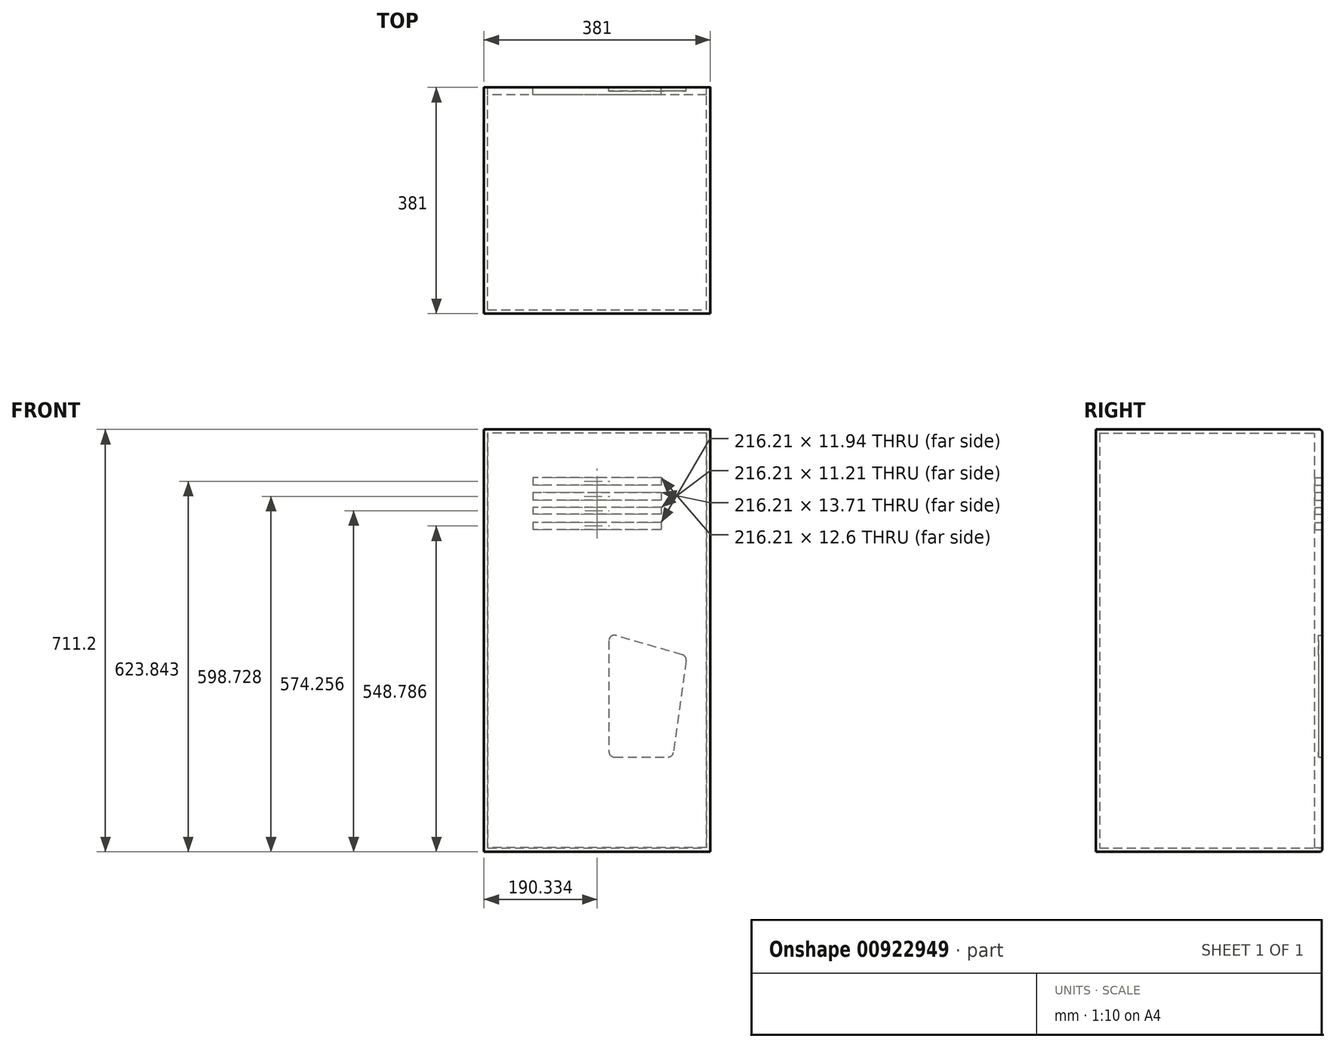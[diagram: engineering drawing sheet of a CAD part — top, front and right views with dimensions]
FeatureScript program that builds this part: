
annotation { "Feature Type Name" : "Feature", "Feature Type Description" : "" }
export const myFeature = defineFeature(function(context is Context, id is Id, definition is map)
    precondition{}
    {
        {
            var Q0;
            Q0=qCreatedBy(makeId("Front.planeOp"),FACE);
            var sketch = newSketch(context, id + "F0", { "sketchPlane" : qUnion([Q0])});
            skLineSegment(sketch, "E0.bottom", {"start": v(-210.3, 429.13) * mm, "end": v(170.7, 429.13) * mm});
            skLineSegment(sketch, "E0.top", {"start": v(-210.3, -282.07) * mm, "end": v(170.7, -282.07) * mm});
            skLineSegment(sketch, "E0.left", {"start": v(-210.3, 429.13) * mm, "end": v(-210.3, -282.07) * mm});
            skLineSegment(sketch, "E0.right", {"start": v(170.7, 429.13) * mm, "end": v(170.7, -282.07) * mm});
            skSolve(sketch);
        }
        {
            var Q0;
            Q0=makeQuery(id+"F0.imprint","IMPRINT",FACE,{"disambiguationData":[TD([[makeQuery(id+"F0.imprint","IMPRINT",EDGE,{"derivedFrom":sQuery(id+"F0.wireOp",EDGE,"E0.bottom")}),-1.0]])]});
            extrude(context, id + "F1", {"entities" : qUnion([Q0]), "endBound" : BoundingType.SYMMETRIC, "depth" : 381 * mm, "offsetDistance" : 25.4 * mm});
        }
        {
            var Q0;
            Q0=makeQuery(id+"F1.opExtrude","CAP_FACE",FACE,{"disambiguationData":[OSD([sQuery(id+"F0.wireOp",EDGE,"E0.bottom"),sQuery(id+"F0.wireOp",EDGE,"E0.top"),sQuery(id+"F0.wireOp",EDGE,"E0.left"),sQuery(id+"F0.wireOp",EDGE,"E0.right")])],"isStart":true});
            shell(context, id + "F2", {"entities" : qUnion([Q0]), "thickness" : 6.35 * mm});
        }
        {
            var Q0;
            Q0=makeQuery(id+"F2.opShell","OFFSET_FACE",FACE,{"disambiguationData":[OSD([sQuery(id+"F0.wireOp",EDGE,"E0.bottom"),sQuery(id+"F0.wireOp",EDGE,"E0.top"),sQuery(id+"F0.wireOp",EDGE,"E0.left"),sQuery(id+"F0.wireOp",EDGE,"E0.right")])]});
            cPlane(context, id + "F3", {"entities" : qUnion([Q0]), "cplaneType" : CPlaneType.OFFSET, "offset" : 368.3 * mm, "width" : 152.4 * mm, "height" : 152.4 * mm});
        }
        {
            var Q0;
            Q0=qCreatedBy(id+"F3.planeOp",FACE);
            var sketch = newSketch(context, id + "F4", { "sketchPlane" : qUnion([Q0])});
            skLineSegment(sketch, "E1.bottom", {"start": v(-168.35, 423.65) * mm, "end": v(206.3, 423.65) * mm});
            skLineSegment(sketch, "E1.top", {"start": v(-168.35, -274.85) * mm, "end": v(206.3, -274.85) * mm});
            skLineSegment(sketch, "E1.left", {"start": v(-168.35, 423.65) * mm, "end": v(-168.35, -274.85) * mm});
            skLineSegment(sketch, "E1.right", {"start": v(206.3, 423.65) * mm, "end": v(206.3, -274.85) * mm});
            skLineSegment(sketch, "E2.bottom", {"start": v(-88.14, 348.07) * mm, "end": v(128.07, 348.07) * mm});
            skLineSegment(sketch, "E2.top", {"start": v(-88.14, 247.5) * mm, "end": v(128.07, 247.5) * mm});
            skLineSegment(sketch, "E2.left", {"start": v(-88.14, 348.07) * mm, "end": v(-88.14, 247.5) * mm});
            skLineSegment(sketch, "E2.right", {"start": v(128.07, 348.07) * mm, "end": v(128.07, 247.5) * mm});
            skLineSegment(sketch, "E3", {"start": v(-88.14, 297.8) * mm, "end": v(128.07, 297.8) * mm});
            skLineSegment(sketch, "E4", {"start": v(128.07, 297.8) * mm, "end": v(128.07, 323.51) * mm});
            skLineSegment(sketch, "E5", {"start": v(128.07, 323.51) * mm, "end": v(-88.14, 323.51) * mm});
            skLineSegment(sketch, "E6", {"start": v(-88.14, 323.51) * mm, "end": v(-88.14, 272.69) * mm});
            skLineSegment(sketch, "E7", {"start": v(-88.14, 272.69) * mm, "end": v(128.07, 272.69) * mm});
            skLineSegment(sketch, "E8", {"start": v(-88.14, 335.47) * mm, "end": v(128.07, 335.47) * mm});
            skLineSegment(sketch, "E9", {"start": v(-88.14, 309.8) * mm, "end": v(128.07, 309.8) * mm});
            skLineSegment(sketch, "E10", {"start": v(-88.14, 286.58) * mm, "end": v(128.07, 286.58) * mm});
            skLineSegment(sketch, "E11", {"start": v(-88.14, 260.75) * mm, "end": v(128.07, 260.75) * mm});
            skSolve(sketch);
        }
        {
            var Q0;
            Q0=makeQuery(id+"F4.imprint","IMPRINT",FACE,{"disambiguationData":[TD([[makeQuery(id+"F4.imprint","IMPRINT",EDGE,{"derivedFrom":sQuery(id+"F4.wireOp",EDGE,"E1.bottom")}),-1.0]])]});
            var Q1;
            {var subQ0=sQuery(id+"F4.wireOp",EDGE,"mHhOSxjr-2zmz-sGzj-NxiS-aYpzAD7VbS2n");Q1=makeQuery(id+"F4.imprint","IMPRINT",FACE,{"disambiguationData":[TD([[makeQuery(id+"F4.imprint","IMPRINT",EDGE,{"derivedFrom":subQ0}),1.0]])]});}
            var Q2;
            {var subQ0=sQuery(id+"F4.wireOp",EDGE,"W4M9WIZb-01p7-x7Fy-zKtJ-qoCmWgGV4v3H");Q2=makeQuery(id+"F4.imprint","IMPRINT",FACE,{"disambiguationData":[TD([[makeQuery(id+"F4.imprint","IMPRINT",EDGE,{"derivedFrom":subQ0}),1.0]])]});}
            var Q3;
            {var subQ0=sQuery(id+"F4.wireOp",EDGE,"E5");Q3=makeQuery(id+"F4.imprint","IMPRINT",FACE,{"disambiguationData":[TD([[makeQuery(id+"F4.imprint","IMPRINT",EDGE,{"derivedFrom":subQ0}),-1.0]])]});}
            var Q4;
            {var subQ0=sQuery(id+"F4.wireOp",EDGE,"E3");Q4=makeQuery(id+"F4.imprint","IMPRINT",FACE,{"disambiguationData":[TD([[makeQuery(id+"F4.imprint","IMPRINT",EDGE,{"derivedFrom":subQ0}),1.0]])]});}
            var Q5;
            {var subQ0=sQuery(id+"F4.wireOp",EDGE,"E7");Q5=makeQuery(id+"F4.imprint","IMPRINT",FACE,{"disambiguationData":[TD([[makeQuery(id+"F4.imprint","IMPRINT",EDGE,{"derivedFrom":subQ0}),1.0]])]});}
            var Q6;
            {var subQ0=sQuery(id+"F4.wireOp",EDGE,"E2.top");Q6=makeQuery(id+"F4.imprint","IMPRINT",FACE,{"disambiguationData":[TD([[makeQuery(id+"F4.imprint","IMPRINT",EDGE,{"derivedFrom":subQ0}),1.0]])]});}
            extrude(context, id + "F5", {"entities" : qUnion([Q0, Q1, Q2, Q3, Q4, Q5, Q6]), "operationType" : NewBodyOperationType.ADD, "endBound" : BoundingType.SYMMETRIC, "oppositeDirection" : true, "depth" : 12.7 * mm, "offsetDistance" : 25.4 * mm});
        }
        {
            var Q0;
            Q0=makeQuery(id+"F1.opExtrude","CAP_EDGE",EDGE,{"disambiguationData":[OSD([sQuery(id+"F0.wireOp",EDGE,"E0.bottom")])],"isStart":true});
            var Q1;
            Q1=makeQuery(id+"F1.opExtrude","CAP_EDGE",EDGE,{"disambiguationData":[OSD([sQuery(id+"F0.wireOp",EDGE,"E0.top")])],"isStart":true});
            fillet(context, id + "F6", {"entities" : qUnion([Q0, Q1]), "radius" : 5.08 * mm, "tangentPropagation" : true, "allowEdgeOverflow" : false});
        }
        {
            var Q0;
            Q0=makeQuery(id+"F5.boolean.opBoolean","MERGE",FACE,{"derivedFrom":[makeQuery(id+"F1.opExtrude","CAP_FACE",FACE,{"disambiguationData":[OSD([sQuery(id+"F0.wireOp",EDGE,"E0.bottom"),sQuery(id+"F0.wireOp",EDGE,"E0.top"),sQuery(id+"F0.wireOp",EDGE,"E0.left"),sQuery(id+"F0.wireOp",EDGE,"E0.right")])],"isStart":true}),makeQuery(id+"F5.opExtrude","CAP_FACE",FACE,{"disambiguationData":[OSD([sQuery(id+"F4.wireOp",EDGE,"E1.bottom"),sQuery(id+"F4.wireOp",EDGE,"E1.top"),sQuery(id+"F4.wireOp",EDGE,"E1.left"),sQuery(id+"F4.wireOp",EDGE,"E1.right"),sQuery(id+"F4.wireOp",EDGE,"E2.bottom"),sQuery(id+"F4.wireOp",EDGE,"E2.left"),sQuery(id+"F4.wireOp",EDGE,"E2.right"),sQuery(id+"F4.wireOp",EDGE,"E3"),sQuery(id+"F4.wireOp",EDGE,"E4"),sQuery(id+"F4.wireOp",EDGE,"E5"),sQuery(id+"F4.wireOp",EDGE,"E6"),sQuery(id+"F4.wireOp",EDGE,"E7"),sQuery(id+"F4.wireOp",EDGE,"E8"),sQuery(id+"F4.wireOp",EDGE,"E9"),sQuery(id+"F4.wireOp",EDGE,"E10"),sQuery(id+"F4.wireOp",EDGE,"E11")])],"isStart":true})]});
            var sketch = newSketch(context, id + "F7", { "sketchPlane" : qUnion([Q0])});
            skLineSegment(sketch, "E12", {"start": v(-130.12, 40) * mm, "end": v(-108.49, -114.68) * mm});
            skLineSegment(sketch, "E13", {"start": v(-123.78, 49.77) * mm, "end": v(-11.36, 82.26) * mm});
            skLineSegment(sketch, "E14", {"start": v(0, 73.72) * mm, "end": v(0, -113.45) * mm});
            skLineSegment(sketch, "E15", {"start": v(-8.89, -122.34) * mm, "end": v(-99.68, -122.34) * mm});
            skPoint(sketch, "E16.visualSharp", {"position": v(-131.19, 47.63) * mm});
            skArc(sketch, "E16.filletArc", {"start": v(-123.78, 49.77) * mm, "mid": v(-128.77, 46.07) * mm, "end": v(-130.12, 40) * mm});
            skPoint(sketch, "E17.visualSharp", {"position": v(0, 85.55) * mm});
            skArc(sketch, "E17.filletArc", {"start": v(0, 73.72) * mm, "mid": v(-3.55, 80.83) * mm, "end": v(-11.36, 82.26) * mm});
            skPoint(sketch, "E18.visualSharp", {"position": v(-107.42, -122.34) * mm});
            skArc(sketch, "E18.filletArc", {"start": v(-108.49, -114.68) * mm, "mid": v(-105.52, -120.16) * mm, "end": v(-99.68, -122.34) * mm});
            skPoint(sketch, "E19.visualSharp", {"position": v(0, -122.34) * mm});
            skArc(sketch, "E19.filletArc", {"start": v(-8.89, -122.34) * mm, "mid": v(-2.6, -119.74) * mm, "end": v(0, -113.45) * mm});
            skSolve(sketch);
        }
        {
            var Q0;
            Q0=makeQuery(id+"F7.imprint","IMPRINT",FACE,{"disambiguationData":[TD([[makeQuery(id+"F7.imprint","IMPRINT",EDGE,{"derivedFrom":sQuery(id+"F7.wireOp",EDGE,"E12")}),1.0]])]});
            extrude(context, id + "F8", {"entities" : qUnion([Q0]), "operationType" : NewBodyOperationType.REMOVE, "oppositeDirection" : true, "depth" : 6.35 * mm, "offsetDistance" : 25.4 * mm});
        }
    });
